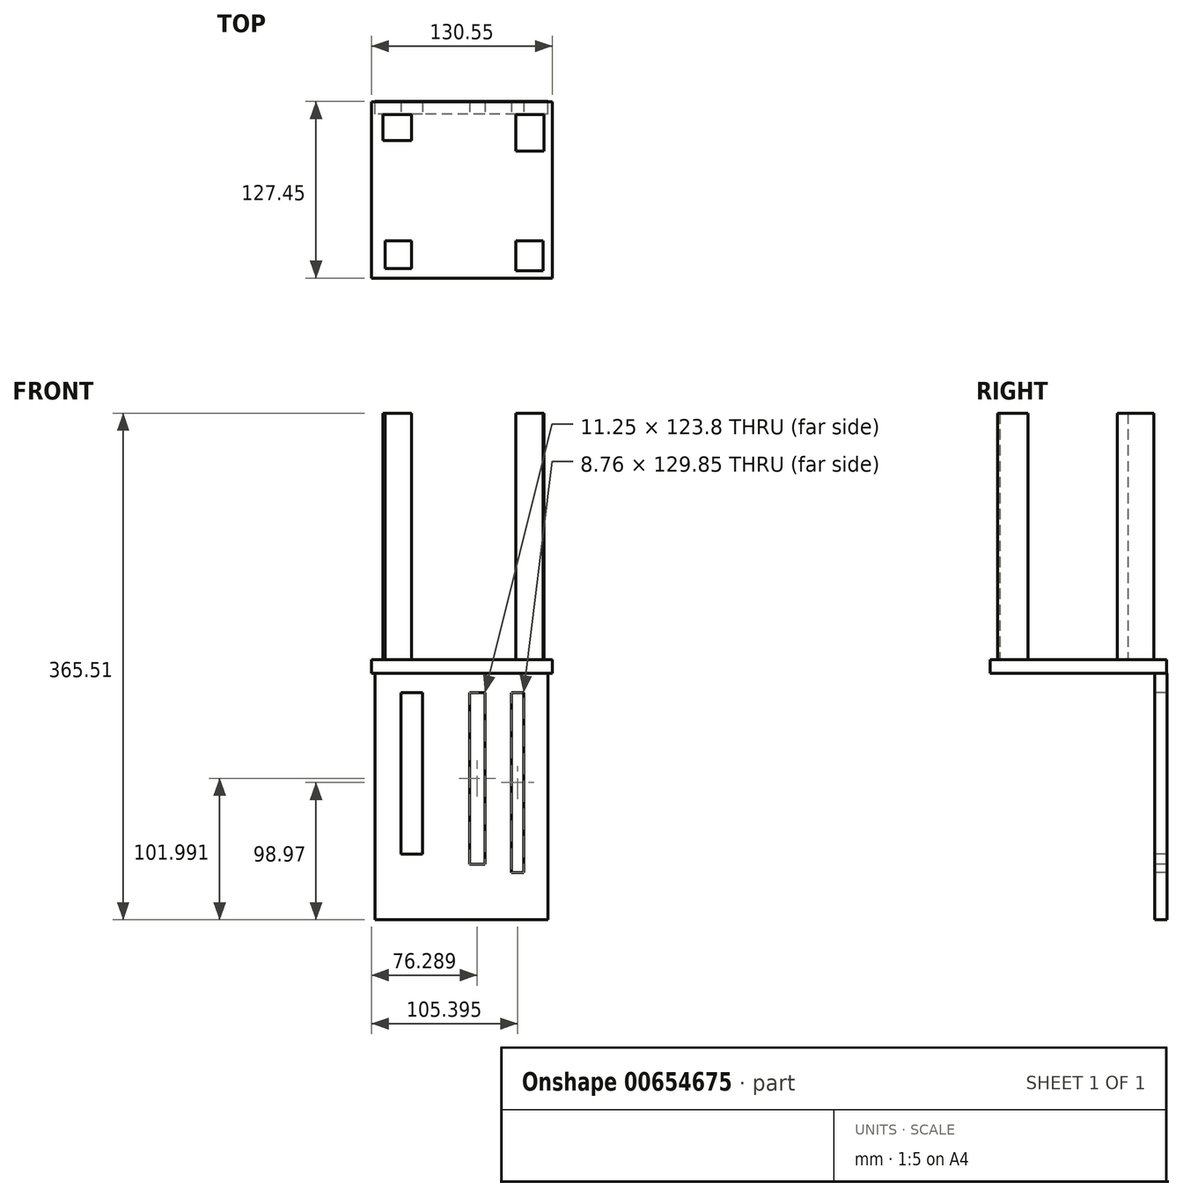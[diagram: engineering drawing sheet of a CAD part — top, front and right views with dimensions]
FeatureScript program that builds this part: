
annotation { "Feature Type Name" : "Feature", "Feature Type Description" : "" }
export const myFeature = defineFeature(function(context is Context, id is Id, definition is map)
    precondition{}
    {
        {
            var Q0;
            Q0=qCreatedBy(makeId("Top.planeOp"),FACE);
            var sketch = newSketch(context, id + "F0", { "sketchPlane" : qUnion([Q0])});
            skLineSegment(sketch, "E0.bottom", {"start": v(-63.02, -59.7) * mm, "end": v(67.53, -59.7) * mm});
            skLineSegment(sketch, "E0.top", {"start": v(-63.02, 67.53) * mm, "end": v(67.53, 67.53) * mm});
            skLineSegment(sketch, "E0.left", {"start": v(-63.02, -59.7) * mm, "end": v(-63.02, 67.53) * mm});
            skLineSegment(sketch, "E0.right", {"start": v(67.53, -59.7) * mm, "end": v(67.53, 67.53) * mm});
            skSolve(sketch);
        }
        {
            var Q0;
            Q0=makeQuery(id+"F0.imprint","IMPRINT",FACE,{"disambiguationData":[TD([[makeQuery(id+"F0.imprint","IMPRINT",EDGE,{"derivedFrom":sQuery(id+"F0.wireOp",EDGE,"E0.bottom")}),1.0]])]});
            extrude(context, id + "F1", {"entities" : qUnion([Q0]), "depth" : 9.9 * mm, "offsetDistance" : 25.4 * mm});
        }
        {
            var Q0;
            Q0=makeQuery(id+"F0.imprint","IMPRINT",FACE,{"disambiguationData":[TD([[makeQuery(id+"F0.imprint","IMPRINT",EDGE,{"derivedFrom":sQuery(id+"F0.wireOp",EDGE,"E0.bottom")}),1.0]])]});
            var sketch = newSketch(context, id + "F2", { "sketchPlane" : qUnion([Q0])});
            skLineSegment(sketch, "E1.bottom", {"start": v(60.8, -54.38) * mm, "end": v(41.07, -54.38) * mm});
            skLineSegment(sketch, "E1.top", {"start": v(60.8, -32.62) * mm, "end": v(41.07, -32.62) * mm});
            skLineSegment(sketch, "E1.left", {"start": v(60.8, -54.38) * mm, "end": v(60.8, -32.62) * mm});
            skLineSegment(sketch, "E1.right", {"start": v(41.07, -54.38) * mm, "end": v(41.07, -32.62) * mm});
            skLineSegment(sketch, "E2.bottom", {"start": v(61.57, 31.95) * mm, "end": v(41.07, 31.95) * mm});
            skLineSegment(sketch, "E2.top", {"start": v(61.57, 58.2) * mm, "end": v(41.07, 58.2) * mm});
            skLineSegment(sketch, "E2.left", {"start": v(61.57, 31.95) * mm, "end": v(61.57, 58.2) * mm});
            skLineSegment(sketch, "E2.right", {"start": v(41.07, 31.95) * mm, "end": v(41.07, 58.2) * mm});
            skLineSegment(sketch, "E3.bottom", {"start": v(-54.66, 58.2) * mm, "end": v(-34.01, 58.2) * mm});
            skLineSegment(sketch, "E3.top", {"start": v(-54.66, 39.53) * mm, "end": v(-34.01, 39.53) * mm});
            skLineSegment(sketch, "E3.left", {"start": v(-54.66, 58.2) * mm, "end": v(-54.66, 39.53) * mm});
            skLineSegment(sketch, "E3.right", {"start": v(-34.01, 58.2) * mm, "end": v(-34.01, 39.53) * mm});
            skLineSegment(sketch, "E4.bottom", {"start": v(-53.06, -52.71) * mm, "end": v(-34.01, -52.71) * mm});
            skLineSegment(sketch, "E4.top", {"start": v(-53.06, -32.62) * mm, "end": v(-34.01, -32.62) * mm});
            skLineSegment(sketch, "E4.left", {"start": v(-53.06, -52.71) * mm, "end": v(-53.06, -32.62) * mm});
            skLineSegment(sketch, "E4.right", {"start": v(-34.01, -52.71) * mm, "end": v(-34.01, -32.62) * mm});
            skSolve(sketch);
        }
        {
            var Q0;
            Q0 = qSketchRegion(id + "F2", true);
            extrude(context, id + "F3", {"entities" : qUnion([Q0]), "operationType" : NewBodyOperationType.ADD, "depth" : 187.7 * mm, "offsetDistance" : 25.4 * mm});
        }
        {
            var Q0;
            Q0=makeQuery(id+"F0.imprint","IMPRINT",FACE,{"disambiguationData":[TD([[makeQuery(id+"F0.imprint","IMPRINT",EDGE,{"derivedFrom":sQuery(id+"F0.wireOp",EDGE,"E0.bottom")}),1.0]])]});
            var sketch = newSketch(context, id + "F4", { "sketchPlane" : qUnion([Q0])});
            skLineSegment(sketch, "E5.bottom", {"start": v(64.17, 58.82) * mm, "end": v(-60.5, 58.82) * mm});
            skLineSegment(sketch, "E5.top", {"start": v(64.17, 67.74) * mm, "end": v(-60.5, 67.74) * mm});
            skLineSegment(sketch, "E5.left", {"start": v(64.17, 58.82) * mm, "end": v(64.17, 67.74) * mm});
            skLineSegment(sketch, "E5.right", {"start": v(-60.5, 58.82) * mm, "end": v(-60.5, 67.74) * mm});
            skLineSegment(sketch, "E6.bottom", {"start": v(64.17, 58.82) * mm, "end": v(64.17, 58.82) * mm});
            skLineSegment(sketch, "E6.top", {"start": v(64.17, 67.74) * mm, "end": v(64.17, 67.74) * mm});
            skSolve(sketch);
        }
        {
            var Q0;
            Q0 = qSketchRegion(id + "F4", true);
            extrude(context, id + "F5", {"entities" : qUnion([Q0]), "operationType" : NewBodyOperationType.ADD, "oppositeDirection" : true, "depth" : 177.8 * mm, "offsetDistance" : 25.4 * mm});
        }
        {
            var Q0;
            Q0=makeQuery(id+"F5.opExtrude","SWEPT_FACE",FACE,{"disambiguationData":[OSD([sQuery(id+"F4.wireOp",EDGE,"E5.bottom")])]});
            var sketch = newSketch(context, id + "F6", { "sketchPlane" : qUnion([Q0])});
            skLineSegment(sketch, "E7.bottom", {"start": v(46.75, -143.75) * mm, "end": v(38, -143.75) * mm});
            skLineSegment(sketch, "E7.top", {"start": v(46.75, -13.9) * mm, "end": v(38, -13.9) * mm});
            skLineSegment(sketch, "E7.left", {"start": v(46.75, -143.75) * mm, "end": v(46.75, -13.9) * mm});
            skLineSegment(sketch, "E7.right", {"start": v(38, -143.75) * mm, "end": v(38, -13.9) * mm});
            skLineSegment(sketch, "E8.bottom", {"start": v(18.9, -137.71) * mm, "end": v(7.64, -137.71) * mm});
            skLineSegment(sketch, "E8.top", {"start": v(18.9, -13.9) * mm, "end": v(7.64, -13.9) * mm});
            skLineSegment(sketch, "E8.left", {"start": v(18.9, -137.71) * mm, "end": v(18.9, -13.9) * mm});
            skLineSegment(sketch, "E8.right", {"start": v(7.64, -137.71) * mm, "end": v(7.64, -13.9) * mm});
            skLineSegment(sketch, "E9.bottom", {"start": v(-26.3, -130.34) * mm, "end": v(-41.84, -130.34) * mm});
            skLineSegment(sketch, "E9.top", {"start": v(-26.3, -13.9) * mm, "end": v(-41.84, -13.9) * mm});
            skLineSegment(sketch, "E9.left", {"start": v(-26.3, -130.34) * mm, "end": v(-26.3, -13.9) * mm});
            skLineSegment(sketch, "E9.right", {"start": v(-41.84, -130.34) * mm, "end": v(-41.84, -13.9) * mm});
            skSolve(sketch);
        }
        {
            var Q0;
            Q0 = qSketchRegion(id + "F6", true);
            extrude(context, id + "F7", {"entities" : qUnion([Q0]), "operationType" : NewBodyOperationType.REMOVE, "oppositeDirection" : true, "depth" : 25.4 * mm, "offsetDistance" : 25.4 * mm});
        }
    });
